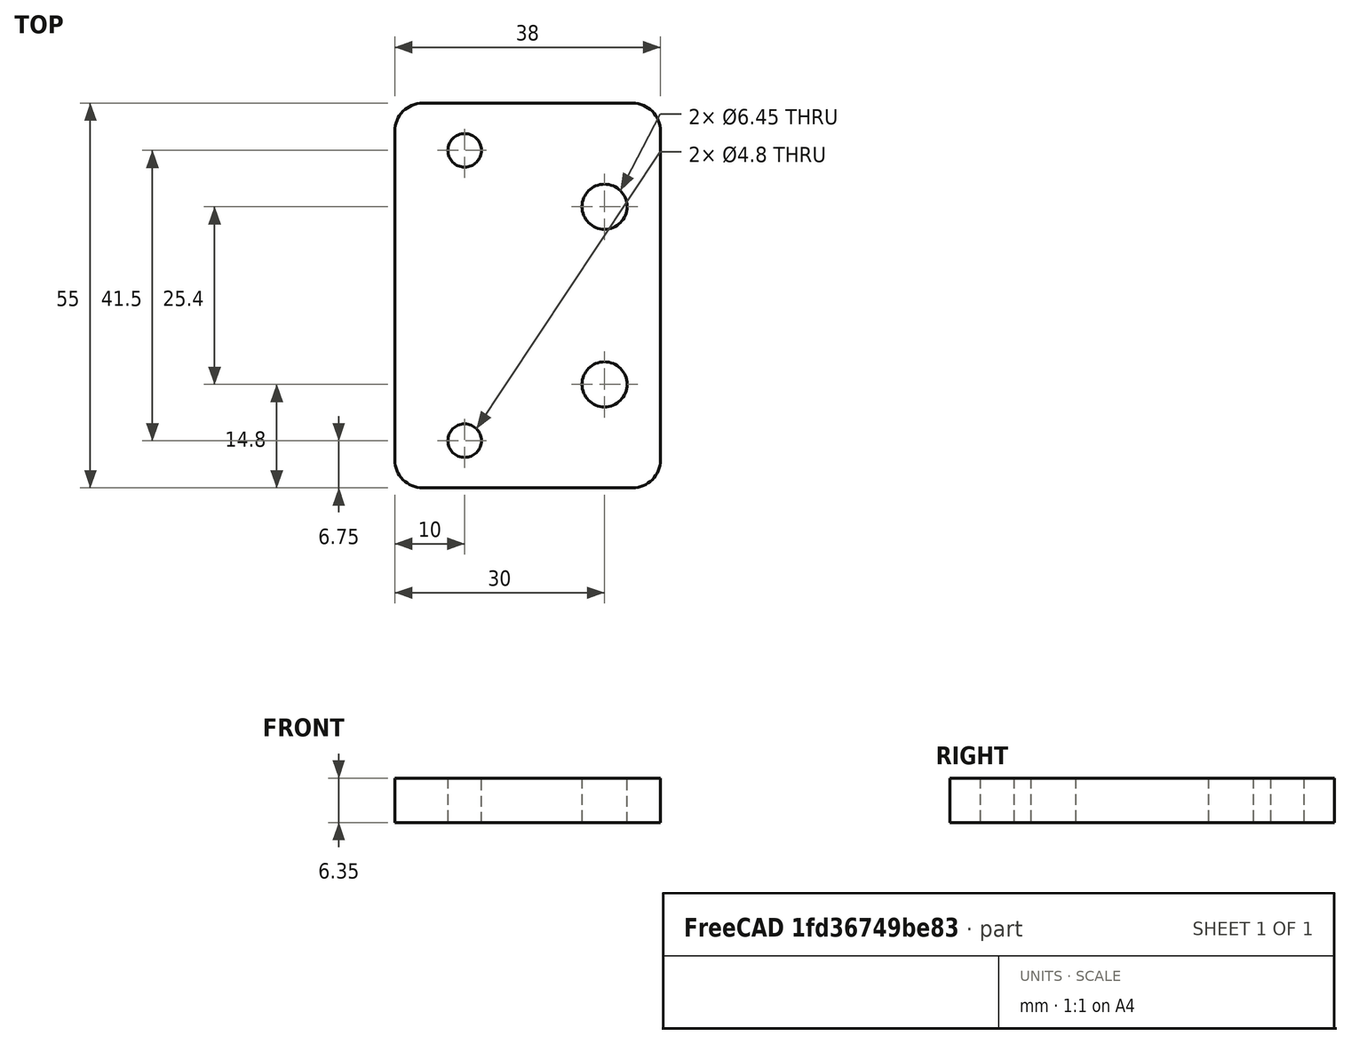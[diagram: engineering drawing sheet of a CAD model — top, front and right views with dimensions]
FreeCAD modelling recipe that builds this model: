
FCSTD DOCUMENT  (FreeCAD 0.21R30691 (Git))
Label: Adapter_Flowmeter_imperial
License: All rights reserved
LicenseURL: http://en.wikipedia.org/wiki/All_rights_reserved
objects: Sketcher::SketchObject×1, PartDesign::Pad×1, PartDesign::Body×1
note: 4 computed .brp shape members not serialized (recipe doc carries the construction recipe); baked Part::Feature solids carry a one-line shape summary decoded from their .brp

FEATURE [Sketcher::SketchObject] Sketch
  FullyConstrained = true
  MapMode = 5
  Support = -> [XY_Plane]
  sketch-geometry (14):
    g0: Circle CenterX=0 CenterY=20.75 CenterZ=0 NormalX=0 NormalY=0 NormalZ=1 AngleXU=0 Radius=2.4
    g1: Circle CenterX=0 CenterY=-20.75 CenterZ=0 NormalX=0 NormalY=0 NormalZ=1 AngleXU=0 Radius=2.4
    g2: Circle CenterX=20 CenterY=12.7 CenterZ=0 NormalX=0 NormalY=0 NormalZ=1 AngleXU=0 Radius=3.225
    g3: Circle CenterX=20 CenterY=-12.7 CenterZ=0 NormalX=0 NormalY=0 NormalZ=1 AngleXU=0 Radius=3.225
    g4: ArcOfCircle CenterX=-6 CenterY=23.5 CenterZ=0 NormalX=0 NormalY=0 NormalZ=1 AngleXU=0 Radius=4 StartAngle=1.5708 EndAngle=3.14159
    g5: LineSegment StartX=-6 StartY=27.5 StartZ=0 EndX=24 EndY=27.5 EndZ=0
    g6: ArcOfCircle CenterX=24 CenterY=23.5 CenterZ=0 NormalX=0 NormalY=0 NormalZ=1 AngleXU=0 Radius=4 StartAngle=5e-16 EndAngle=1.5708
    g7: LineSegment StartX=28 StartY=23.5 StartZ=0 EndX=28 EndY=-23.5 EndZ=0
    g8: ArcOfCircle CenterX=24 CenterY=-23.5 CenterZ=0 NormalX=0 NormalY=0 NormalZ=1 AngleXU=0 Radius=4 StartAngle=4.71239 EndAngle=6.28319
    g9: LineSegment StartX=24 StartY=-27.5 StartZ=0 EndX=-6 EndY=-27.5 EndZ=0
    g10: ArcOfCircle CenterX=-6 CenterY=-23.5 CenterZ=0 NormalX=0 NormalY=0 NormalZ=1 AngleXU=0 Radius=4 StartAngle=3.14159 EndAngle=4.71239
    g11: LineSegment StartX=-10 StartY=-23.5 StartZ=0 EndX=-10 EndY=23.5 EndZ=0
    g12: GeomPoint X=-10 Y=27.5 Z=0
    g13: GeomPoint X=28 Y=-27.5 Z=0
  constraints (33):
    c: PointOnObject(g0,g-2)
    c: Equal(g0,g1)
    c: Diameter(g0) = 4.8
    c: DistanceY(g1,g0) = 41.5
    c: Symmetric(g0,g1,g-1)
    c: Equal(g3,g2)
    c: Diameter(g3) = 6.45
    c: DistanceY(g3,g2) = 25.4
    c: Symmetric(g2,g3,g-1)
    c: DistanceX(g-1,g2) = 20
    c: Tangent(g4,g5) = 1.5708
    c: Tangent(g5,g6) = 1.5708
    c: Tangent(g6,g7) = 1.5708
    c: Tangent(g7,g8) = 1.5708
    c: Tangent(g8,g9) = 1.5708
    c: Tangent(g9,g10) = 1.5708
    c: Tangent(g10,g11) = 1.5708
    c: Tangent(g11,g4) = 1.5708
    c: Horizontal(g5)
    c: Horizontal(g9)
    c: Vertical(g7)
    c: Vertical(g11)
    c: Equal(g4,g6)
    c: Equal(g6,g8)
    c: PointOnObject(g12,g5)
    c: PointOnObject(g12,g11)
    c: PointOnObject(g13,g7)
    c: PointOnObject(g13,g9)
    c: DistanceY(g9,g4) = 55
    c: Symmetric(g4,g9,g-1)
    c: Diameter(g6) = 8
    c: DistanceX(g2,g6) = 8
    c: DistanceX(g4,g0) = 10
FEATURE [PartDesign::Pad] Pad
  Direction = (0,0,1)
  Length = 6.35
  Length2 = 10
  Profile = -> Sketch
  ReferenceAxis = -> Sketch [N_Axis]
  Type = 0
FEATURE [PartDesign::Body] Body  label="10-32 to 0.25"
  Group = -> [Sketch,Pad]
  Origin = -> Origin
  Tip = -> Pad
